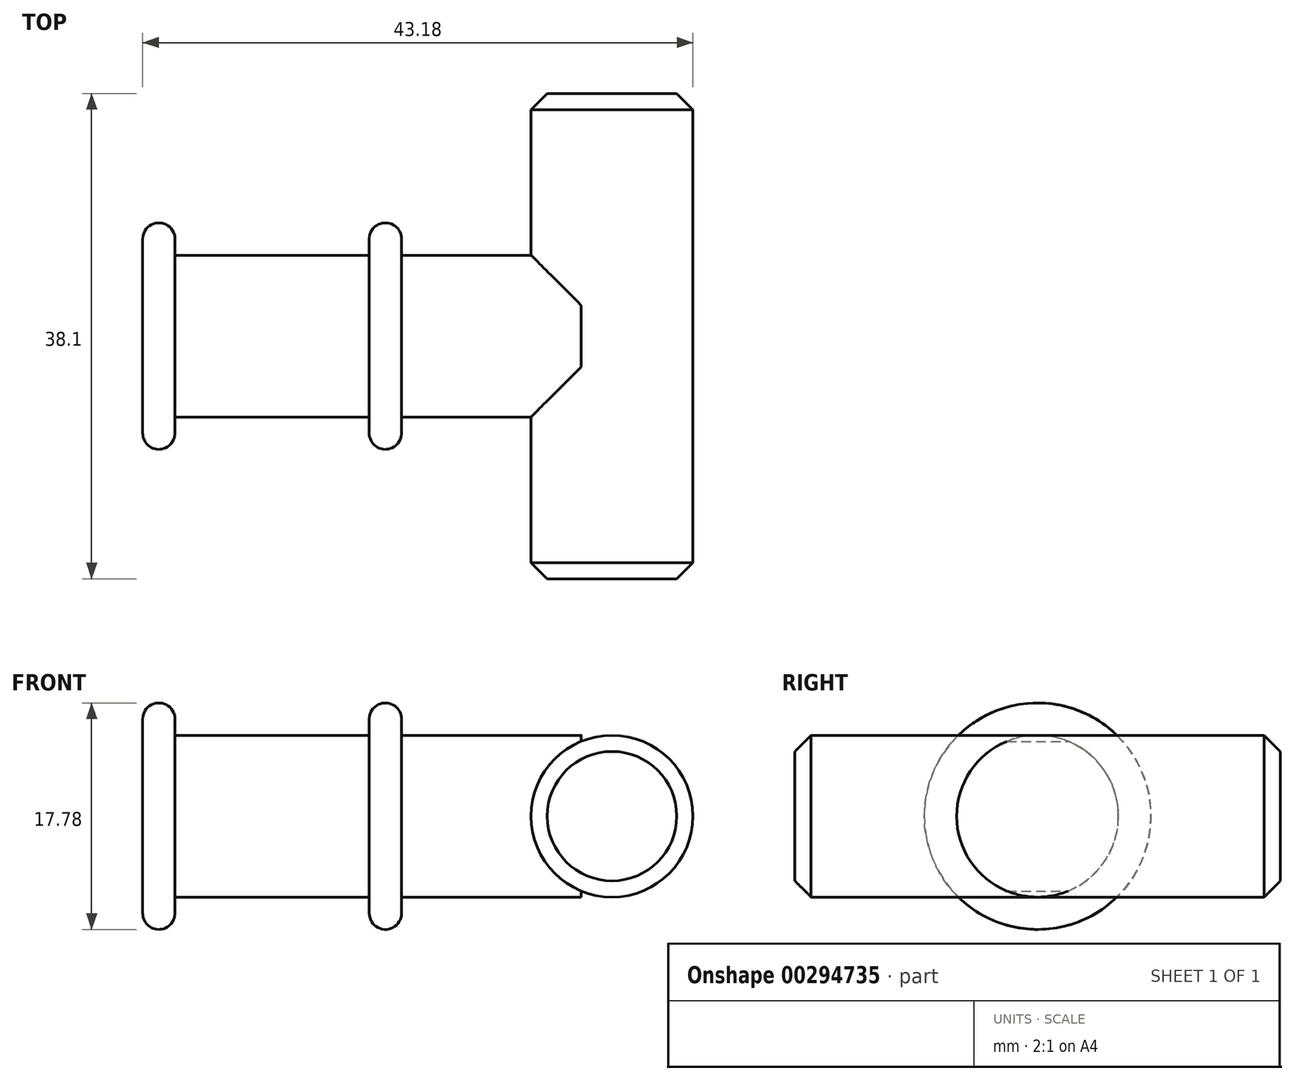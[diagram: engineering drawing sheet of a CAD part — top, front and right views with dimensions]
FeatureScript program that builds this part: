
annotation { "Feature Type Name" : "Feature", "Feature Type Description" : "" }
export const myFeature = defineFeature(function(context is Context, id is Id, definition is map)
    precondition{}
    {
        {
            var Q0;
            Q0=qCreatedBy(makeId("Right.planeOp"),FACE);
            var sketch = newSketch(context, id + "F0", { "sketchPlane" : qUnion([Q0])});
            skCircle(sketch, "E0", {"center": v(0, 182.4) * mm, "radius": 6.35 * mm});
            skSolve(sketch);
        }
        {
            var Q0;
            Q0=qSketchRegion(id+"F0",true);
            extrude(context, id + "F1", {"entities" : qUnion([Q0]), "depth" : 15.24 * mm});
        }
        {
            var Q0;
            Q0=makeQuery(id+"F1.opExtrude","CAP_FACE",FACE,{"disambiguationData":[OSD([sQuery(id+"F0.wireOp",EDGE,"E0")])],"isStart":true});
            var sketch = newSketch(context, id + "F2", { "sketchPlane" : qUnion([Q0])});
            skCircle(sketch, "E1", {"center": v(0, 182.4) * mm, "radius": 8.9 * mm});
            skSolve(sketch);
        }
        {
            var Q0;
            Q0=qSketchRegion(id+"F2",true);
            extrude(context, id + "F3", {"entities" : qUnion([Q0]), "operationType" : NewBodyOperationType.ADD, "depth" : 2.54 * mm});
        }
        {
            var Q0;
            Q0=makeQuery(id+"F3.opExtrude","SWEPT_FACE",FACE,{"disambiguationData":[OSD([sQuery(id+"F2.wireOp",EDGE,"E1")])]});
            fillet(context, id + "F4", {"entities" : qUnion([Q0]), "radius" : 1.27 * mm, "tangentPropagation" : true, "allowEdgeOverflow" : false});
        }
        {
            var Q0;
            Q0=makeQuery(id+"F1.opExtrude","CAP_FACE",FACE,{"disambiguationData":[OSD([sQuery(id+"F0.wireOp",EDGE,"E0")])],"isStart":false});
            var sketch = newSketch(context, id + "F5", { "sketchPlane" : qUnion([Q0])});
            skCircle(sketch, "E2", {"center": v(0, 182.4) * mm, "radius": 8.9 * mm});
            skSolve(sketch);
        }
        {
            var Q0;
            Q0=qSketchRegion(id+"F5",true);
            extrude(context, id + "F6", {"entities" : qUnion([Q0]), "operationType" : NewBodyOperationType.ADD, "depth" : 2.54 * mm});
        }
        {
            var Q0;
            Q0=makeQuery(id+"F6.opExtrude","SWEPT_FACE",FACE,{"disambiguationData":[OSD([sQuery(id+"F5.wireOp",EDGE,"E2")])]});
            fillet(context, id + "F7", {"entities" : qUnion([Q0]), "radius" : 1.27 * mm, "tangentPropagation" : true, "allowEdgeOverflow" : false});
        }
        {
            var Q0;
            Q0=qCreatedBy(makeId("Front.planeOp"),FACE);
            var sketch = newSketch(context, id + "F8", { "sketchPlane" : qUnion([Q0])});
            skCircle(sketch, "E3", {"center": v(34.3, 182.4) * mm, "radius": 6.35 * mm});
            skSolve(sketch);
        }
        {
            var Q0;
            Q0=qSketchRegion(id+"F8",true);
            extrude(context, id + "F9", {"entities" : qUnion([Q0]), "endBound" : BoundingType.SYMMETRIC, "depth" : 38.1 * mm});
        }
        {
            var Q0;
            Q0=makeQuery(id+"F6.opExtrude","CAP_FACE",FACE,{"disambiguationData":[OSD([sQuery(id+"F5.wireOp",EDGE,"E2")])],"isStart":false});
            var sketch = newSketch(context, id + "F10", { "sketchPlane" : qUnion([Q0])});
            skCircle(sketch, "E4", {"center": v(0, 182.4) * mm, "radius": 6.35 * mm});
            skSolve(sketch);
        }
        {
            var Q0;
            Q0=qSketchRegion(id+"F10",true);
            var Q1;
            Q1=sQuery(id+"F10.wireOp",EDGE,"E4");
            extrude(context, id + "F11", {"entities" : qUnion([Q0]), "operationType" : NewBodyOperationType.ADD, "surfaceEntities" : qUnion([Q1]), "depth" : 14.1 * mm});
        }
        {
            var Q0;
            Q0=makeQuery(id+"F9.opExtrude","CAP_EDGE",EDGE,{"disambiguationData":[OSD([sQuery(id+"F8.wireOp",EDGE,"E3")])],"isStart":false});
            var Q1;
            Q1=makeQuery(id+"F9.opExtrude","CAP_EDGE",EDGE,{"disambiguationData":[OSD([sQuery(id+"F8.wireOp",EDGE,"E3")])],"isStart":true});
            chamfer(context, id + "F12", {"entities" : qUnion([Q0, Q1]), "width" : 1.27 * mm, "tangentPropagation" : true});
        }
        {
            var Q0;
            Q0=qCreatedBy(makeId("Front.planeOp"),FACE);
            var sketch = newSketch(context, id + "F13", { "sketchPlane" : qUnion([Q0])});
            skPoint(sketch, "E5", {"position": v(15.24, 182.4) * mm});
            skLineSegment(sketch, "E6", {"start": v(15.24, 182.4) * mm, "end": v(0, 0) * mm, "construction": true});
            skSolve(sketch);
        }
        {
            var Q0;
            Q0=makeQuery(id+"F1.opExtrude","SWEPT_BODY",BODY,{"disambiguationData":[OSD([sQuery(id+"F0.wireOp",EDGE,"E0")])]});
            var Q1;
            Q1=sQuery(id+"F13.wireOp",EDGE,"E6");
            transform(context, id + "F14", {"entities" : qUnion([Q0]), "transformType" : TransformType.TRANSLATION_ENTITY, "oppositeDirectionEntity" : false, "transformLine" : qUnion([Q1]), "makeCopy" : false});
        }
    });
